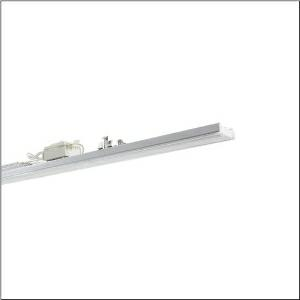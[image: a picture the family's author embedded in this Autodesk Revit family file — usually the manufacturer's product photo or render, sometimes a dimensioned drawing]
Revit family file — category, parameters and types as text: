
# Revit family: licross_21_recessed_mo_51te18vn445g
name_source: partatom
category: Lighting Fixtures
units: mm (PartAtom-declared; Revit-internal decimal feet)

## family parameters
Cut with Voids When Loaded = No
Host = Face
Light Source = No
Part Type = Normal
Room Calculation Point = No
Round Connector Dimension = Use Diameter
Shared = No

## types (1)
- --- (1 x LED, 4500 lm, 24.6 W, 4000K)
    Apparent Load = 25 VA
    CIE Flux Codes = 83 96 99 100 100
    Color Rendering = 80
    Color Temperature = 4000K
    Default Elevation = 1800 mm
    Description = Licross 21 Recessed MO, luminaire insert, of sheet steel, galvanised, coil coated, white, length: 1.500mm, width: 66mm, height: 67mm, LED rated luminous flux: 4.500lm, light colour: 840, SDCM (Standard Deviation of Colour Matching)MacAdam ≤ 2 SDCM (initial), control gear: DALI 2, CLO, with plug, 5-pole, with phase selection, mains connection: 220..240V, AC, 50/60Hz, start of lifetime: 25W, end of service life: 27W, internal wiring halogen-free, primary light control with lens, of plastic, primary optical cover: cover, of PMMA, light emission: direct distribution, primary light characteristic: symmetric, protection rating (complete): IP54, insulation class (complete): insulation class I (protective earthing), certification: CE, ENEC, VDE, UKCA, protection symbol: D if used in an environment with non-conductive dust loads with corresponding accessories, impact resistance: IK06, permissible ambient temperature for indoor applications: -25..+45°C, corresponds to IFS (International Featured Standards) requirements for safety and quality in the food industry, reducing of maximum allowable ambient temperature of 5°C with ceiling mounting, LABS conformity tested according to VDMA 24364:2018-05, The light source and the operating device comply with the requirements of the Ecodesign Regulation (EU) 2019/2020 and are replaceable in accordance with this regulation, packaging unit: 1 piece
    Height = 58 mm
    Lamp = 1 x LED
    Lamp Light Flux = 4500 lm
    Lamp Power = 24.6 W
    Lamp count = 1
    Length = 1500 mm
    Luminous efficacy = 183 lm/W
    Manufacturer = Siteco
    ModVariant = No
    Model = 51TE18VN445G
    Mounting Place = Ceiling
    Mounting Type = Pendant
    Number of Poles = 1
    OnlyDefault = Yes
    Power Factor = 1
    Product Name = Licross 21 Recessed MO
    Product group = luminaire insert | ceiling pendant
    ProductGroupID = 901
    Protection Class = Protection class I
    Protection Degree = IP 54
    RLX_Detail_Level = 1
    RLX_Emergency_Light_Flux = 0 lm
    RLX_Emergency_Type = 0
    RLX_Emergency_Type_DB = No
    RlxData = <blob elided: 24537 chars, md5=68579194>
    Socket = socket
    Standby Power = 0 W
    System Light Flux = 4500 lm
    System Power = 25 W
    Type Comments = factory setting: luminous flux: 100 % | dim-lin: 254 | 163 mA
    Type Image = l_1296930.jpg
    URL = http://relux.com
    VarID = @adj_092439
    Voltage = 0 V
    Weight = 0.00 kg
    Width = 66 mm

## geometry (parser evidence)
native form markers: Blend x4, Sweep x10
no freeform markers — native parametric forms only
